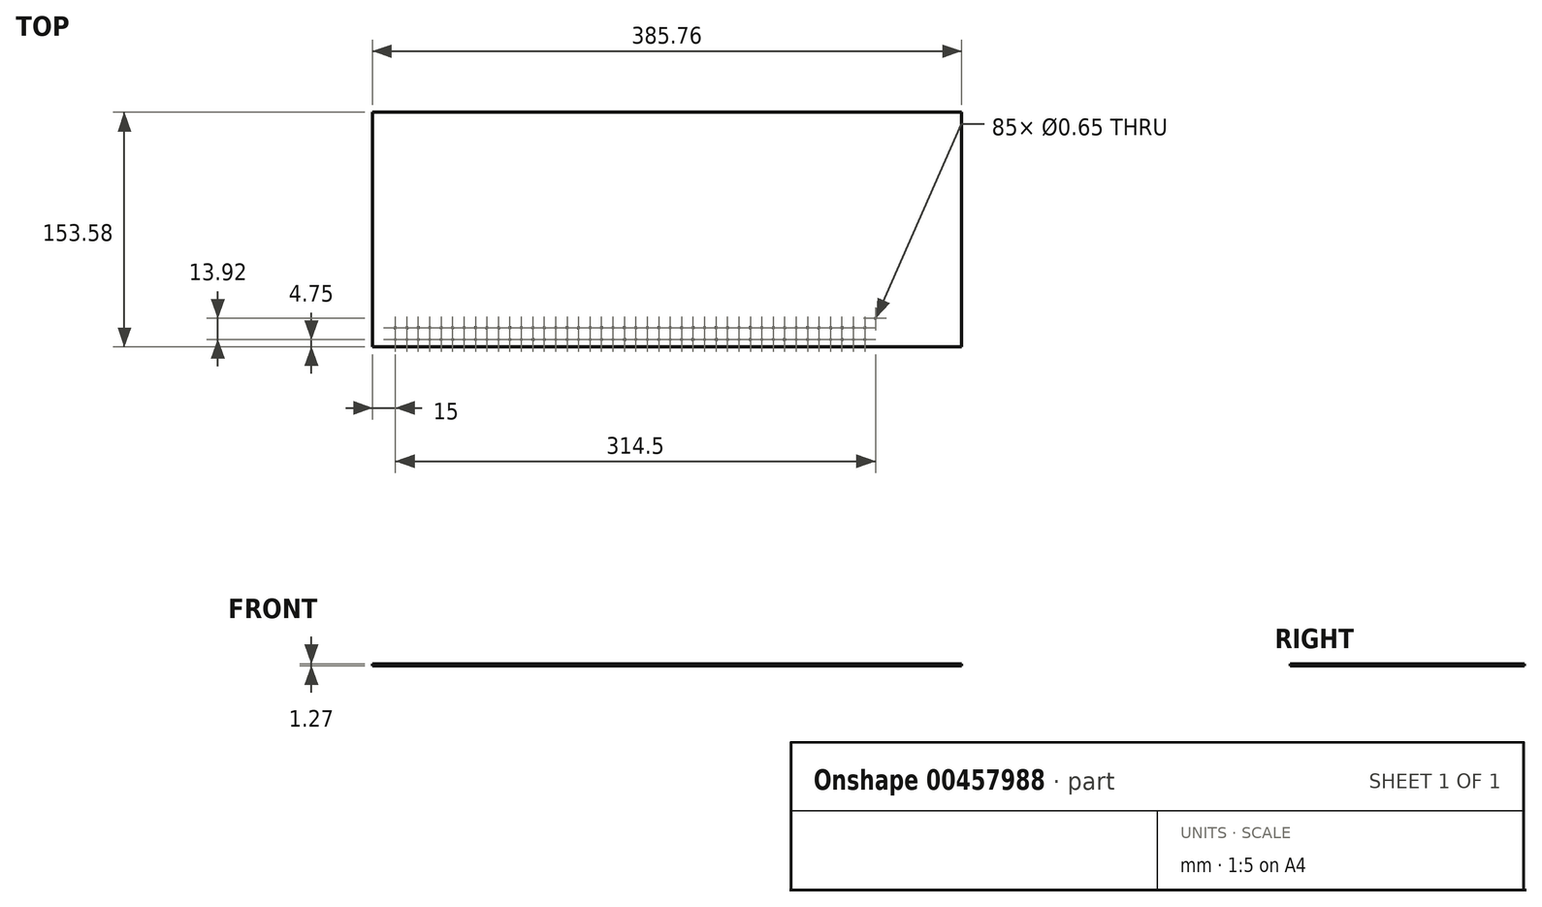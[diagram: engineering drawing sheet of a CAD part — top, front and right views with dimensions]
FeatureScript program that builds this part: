
annotation { "Feature Type Name" : "Feature", "Feature Type Description" : "" }
export const myFeature = defineFeature(function(context is Context, id is Id, definition is map)
    precondition{}
    {
        {
            var Q0;
            Q0=qCreatedBy(makeId("Top.planeOp"),FACE);
            var sketch = newSketch(context, id + "F0", { "sketchPlane" : qUnion([Q0])});
            skLineSegment(sketch, "E0", {"start": v(0, 0) * mm, "end": v(-210, 0) * mm, "construction": true});
            skLineSegment(sketch, "E1", {"start": v(0, 0) * mm, "end": v(175.76, 0) * mm, "construction": true});
            skLineSegment(sketch, "E2", {"start": v(-210, 0) * mm, "end": v(-210, -130) * mm, "construction": true});
            skLineSegment(sketch, "E3", {"start": v(-210, 0) * mm, "end": v(-210, 23.58) * mm, "construction": true});
            skLineSegment(sketch, "E4.bottom", {"start": v(-210, -130) * mm, "end": v(175.76, -130) * mm});
            skLineSegment(sketch, "E4.top", {"start": v(-210, 23.58) * mm, "end": v(175.76, 23.58) * mm});
            skLineSegment(sketch, "E4.left", {"start": v(-210, -130) * mm, "end": v(-210, 23.58) * mm});
            skLineSegment(sketch, "E4.right", {"start": v(175.76, -130) * mm, "end": v(175.76, 23.58) * mm});
            skCircle(sketch, "E5", {"center": v(-195, -117.55) * mm, "radius": 0.33 * mm});
            skCircle(sketch, "E6", {"center": v(-187.5, -117.55) * mm, "radius": 0.33 * mm});
            skCircle(sketch, "E7", {"center": v(-187.5, -125.25) * mm, "radius": 0.33 * mm});
            skCircle(sketch, "E8", {"center": v(-195, -125.25) * mm, "radius": 0.33 * mm});
            skCircle(sketch, "E9.1.0.0", {"center": v(-180, -117.55) * mm, "radius": 0.33 * mm});
            skCircle(sketch, "E9.2.0.0", {"center": v(-165, -117.55) * mm, "radius": 0.33 * mm});
            skCircle(sketch, "E9.3.0.0", {"center": v(-150, -117.55) * mm, "radius": 0.33 * mm});
            skCircle(sketch, "E9.4.0.0", {"center": v(-135, -117.55) * mm, "radius": 0.33 * mm});
            skCircle(sketch, "E9.5.0.0", {"center": v(-120, -117.55) * mm, "radius": 0.33 * mm});
            skCircle(sketch, "E9.6.0.0", {"center": v(-105, -117.55) * mm, "radius": 0.33 * mm});
            skCircle(sketch, "E9.7.0.0", {"center": v(-90, -117.55) * mm, "radius": 0.33 * mm});
            skCircle(sketch, "E9.8.0.0", {"center": v(-75, -117.55) * mm, "radius": 0.33 * mm});
            skCircle(sketch, "E9.9.0.0", {"center": v(-60, -117.55) * mm, "radius": 0.33 * mm});
            skCircle(sketch, "E9.10.0.0", {"center": v(-45, -117.55) * mm, "radius": 0.33 * mm});
            skCircle(sketch, "E9.11.0.0", {"center": v(-30, -117.55) * mm, "radius": 0.33 * mm});
            skCircle(sketch, "E9.12.0.0", {"center": v(-15, -117.55) * mm, "radius": 0.33 * mm});
            skCircle(sketch, "E9.13.0.0", {"center": v(0, -117.55) * mm, "radius": 0.33 * mm});
            skCircle(sketch, "E9.14.0.0", {"center": v(15, -117.55) * mm, "radius": 0.33 * mm});
            skCircle(sketch, "E9.15.0.0", {"center": v(30, -117.55) * mm, "radius": 0.33 * mm});
            skCircle(sketch, "E9.16.0.0", {"center": v(45, -117.55) * mm, "radius": 0.33 * mm});
            skCircle(sketch, "E9.17.0.0", {"center": v(60, -117.55) * mm, "radius": 0.33 * mm});
            skCircle(sketch, "E9.18.0.0", {"center": v(75, -117.55) * mm, "radius": 0.33 * mm});
            skCircle(sketch, "E9.19.0.0", {"center": v(90, -117.55) * mm, "radius": 0.33 * mm});
            skCircle(sketch, "E9.20.0.0", {"center": v(105, -117.55) * mm, "radius": 0.33 * mm});
            skLineSegment(sketch, "E9.direction1", {"start": v(-195, -117.55) * mm, "end": v(-180, -117.55) * mm, "construction": true});
            skCircle(sketch, "E10.1.0.0", {"center": v(-172.5, -117.55) * mm, "radius": 0.33 * mm});
            skCircle(sketch, "E10.2.0.0", {"center": v(-157.5, -117.55) * mm, "radius": 0.33 * mm});
            skCircle(sketch, "E10.3.0.0", {"center": v(-142.5, -117.55) * mm, "radius": 0.33 * mm});
            skCircle(sketch, "E10.4.0.0", {"center": v(-127.5, -117.55) * mm, "radius": 0.33 * mm});
            skCircle(sketch, "E10.5.0.0", {"center": v(-112.5, -117.55) * mm, "radius": 0.33 * mm});
            skCircle(sketch, "E10.6.0.0", {"center": v(-97.5, -117.55) * mm, "radius": 0.33 * mm});
            skCircle(sketch, "E10.7.0.0", {"center": v(-82.5, -117.55) * mm, "radius": 0.33 * mm});
            skCircle(sketch, "E10.8.0.0", {"center": v(-67.5, -117.55) * mm, "radius": 0.33 * mm});
            skCircle(sketch, "E10.9.0.0", {"center": v(-52.5, -117.55) * mm, "radius": 0.33 * mm});
            skCircle(sketch, "E10.10.0.0", {"center": v(-37.5, -117.55) * mm, "radius": 0.33 * mm});
            skCircle(sketch, "E10.11.0.0", {"center": v(-22.5, -117.55) * mm, "radius": 0.33 * mm});
            skCircle(sketch, "E10.12.0.0", {"center": v(-7.5, -117.55) * mm, "radius": 0.33 * mm});
            skCircle(sketch, "E10.13.0.0", {"center": v(7.5, -117.55) * mm, "radius": 0.33 * mm});
            skCircle(sketch, "E10.14.0.0", {"center": v(22.5, -117.55) * mm, "radius": 0.33 * mm});
            skCircle(sketch, "E10.15.0.0", {"center": v(37.5, -117.55) * mm, "radius": 0.33 * mm});
            skCircle(sketch, "E10.16.0.0", {"center": v(52.5, -117.55) * mm, "radius": 0.33 * mm});
            skCircle(sketch, "E10.17.0.0", {"center": v(67.5, -117.55) * mm, "radius": 0.33 * mm});
            skCircle(sketch, "E10.18.0.0", {"center": v(82.5, -117.55) * mm, "radius": 0.33 * mm});
            skCircle(sketch, "E10.19.0.0", {"center": v(97.5, -117.55) * mm, "radius": 0.33 * mm});
            skCircle(sketch, "E10.20.0.0", {"center": v(112.5, -117.55) * mm, "radius": 0.33 * mm});
            skLineSegment(sketch, "E10.direction1", {"start": v(-187.5, -117.55) * mm, "end": v(-172.5, -117.55) * mm, "construction": true});
            skCircle(sketch, "E11.1.0.0", {"center": v(-180, -125.25) * mm, "radius": 0.33 * mm});
            skCircle(sketch, "E11.2.0.0", {"center": v(-165, -125.25) * mm, "radius": 0.33 * mm});
            skCircle(sketch, "E11.3.0.0", {"center": v(-150, -125.25) * mm, "radius": 0.33 * mm});
            skCircle(sketch, "E11.4.0.0", {"center": v(-135, -125.25) * mm, "radius": 0.33 * mm});
            skCircle(sketch, "E11.5.0.0", {"center": v(-120, -125.25) * mm, "radius": 0.33 * mm});
            skCircle(sketch, "E11.6.0.0", {"center": v(-105, -125.25) * mm, "radius": 0.33 * mm});
            skCircle(sketch, "E11.7.0.0", {"center": v(-90, -125.25) * mm, "radius": 0.33 * mm});
            skCircle(sketch, "E11.8.0.0", {"center": v(-75, -125.25) * mm, "radius": 0.33 * mm});
            skCircle(sketch, "E11.9.0.0", {"center": v(-60, -125.25) * mm, "radius": 0.33 * mm});
            skCircle(sketch, "E11.10.0.0", {"center": v(-45, -125.25) * mm, "radius": 0.33 * mm});
            skCircle(sketch, "E11.11.0.0", {"center": v(-30, -125.25) * mm, "radius": 0.33 * mm});
            skCircle(sketch, "E11.12.0.0", {"center": v(-15, -125.25) * mm, "radius": 0.33 * mm});
            skCircle(sketch, "E11.13.0.0", {"center": v(0, -125.25) * mm, "radius": 0.33 * mm});
            skCircle(sketch, "E11.14.0.0", {"center": v(15, -125.25) * mm, "radius": 0.33 * mm});
            skCircle(sketch, "E11.15.0.0", {"center": v(30, -125.25) * mm, "radius": 0.33 * mm});
            skCircle(sketch, "E11.16.0.0", {"center": v(45, -125.25) * mm, "radius": 0.33 * mm});
            skCircle(sketch, "E11.17.0.0", {"center": v(60, -125.25) * mm, "radius": 0.33 * mm});
            skCircle(sketch, "E11.18.0.0", {"center": v(75, -125.25) * mm, "radius": 0.33 * mm});
            skCircle(sketch, "E11.19.0.0", {"center": v(90, -125.25) * mm, "radius": 0.33 * mm});
            skCircle(sketch, "E11.20.0.0", {"center": v(105, -125.25) * mm, "radius": 0.33 * mm});
            skLineSegment(sketch, "E11.direction1", {"start": v(-195, -125.25) * mm, "end": v(-180, -125.25) * mm, "construction": true});
            skCircle(sketch, "E12.1.0.0", {"center": v(-172.5, -125.25) * mm, "radius": 0.33 * mm});
            skCircle(sketch, "E12.2.0.0", {"center": v(-157.5, -125.25) * mm, "radius": 0.33 * mm});
            skCircle(sketch, "E12.3.0.0", {"center": v(-142.5, -125.25) * mm, "radius": 0.33 * mm});
            skCircle(sketch, "E12.4.0.0", {"center": v(-127.5, -125.25) * mm, "radius": 0.33 * mm});
            skCircle(sketch, "E12.5.0.0", {"center": v(-112.5, -125.25) * mm, "radius": 0.33 * mm});
            skCircle(sketch, "E12.6.0.0", {"center": v(-97.5, -125.25) * mm, "radius": 0.33 * mm});
            skCircle(sketch, "E12.7.0.0", {"center": v(-82.5, -125.25) * mm, "radius": 0.33 * mm});
            skCircle(sketch, "E12.8.0.0", {"center": v(-67.5, -125.25) * mm, "radius": 0.33 * mm});
            skCircle(sketch, "E12.9.0.0", {"center": v(-52.5, -125.25) * mm, "radius": 0.33 * mm});
            skCircle(sketch, "E12.10.0.0", {"center": v(-37.5, -125.25) * mm, "radius": 0.33 * mm});
            skCircle(sketch, "E12.11.0.0", {"center": v(-22.5, -125.25) * mm, "radius": 0.33 * mm});
            skCircle(sketch, "E12.12.0.0", {"center": v(-7.5, -125.25) * mm, "radius": 0.33 * mm});
            skCircle(sketch, "E12.13.0.0", {"center": v(7.5, -125.25) * mm, "radius": 0.33 * mm});
            skCircle(sketch, "E12.14.0.0", {"center": v(22.5, -125.25) * mm, "radius": 0.33 * mm});
            skCircle(sketch, "E12.15.0.0", {"center": v(37.5, -125.25) * mm, "radius": 0.33 * mm});
            skCircle(sketch, "E12.16.0.0", {"center": v(52.5, -125.25) * mm, "radius": 0.33 * mm});
            skCircle(sketch, "E12.17.0.0", {"center": v(67.5, -125.25) * mm, "radius": 0.33 * mm});
            skCircle(sketch, "E12.18.0.0", {"center": v(82.5, -125.25) * mm, "radius": 0.33 * mm});
            skCircle(sketch, "E12.19.0.0", {"center": v(97.5, -125.25) * mm, "radius": 0.33 * mm});
            skCircle(sketch, "E12.20.0.0", {"center": v(112.5, -125.25) * mm, "radius": 0.33 * mm});
            skLineSegment(sketch, "E12.direction1", {"start": v(-187.5, -125.25) * mm, "end": v(-172.5, -125.25) * mm, "construction": true});
            skCircle(sketch, "E13", {"center": v(119.5, -111.33) * mm, "radius": 0.33 * mm});
            skSolve(sketch);
        }
        {
            var Q0;
            Q0 = qSketchRegion(id + "F0", true);
            extrude(context, id + "F1", {"entities" : qUnion([Q0]), "depth" : 1.27 * mm});
        }
    });
